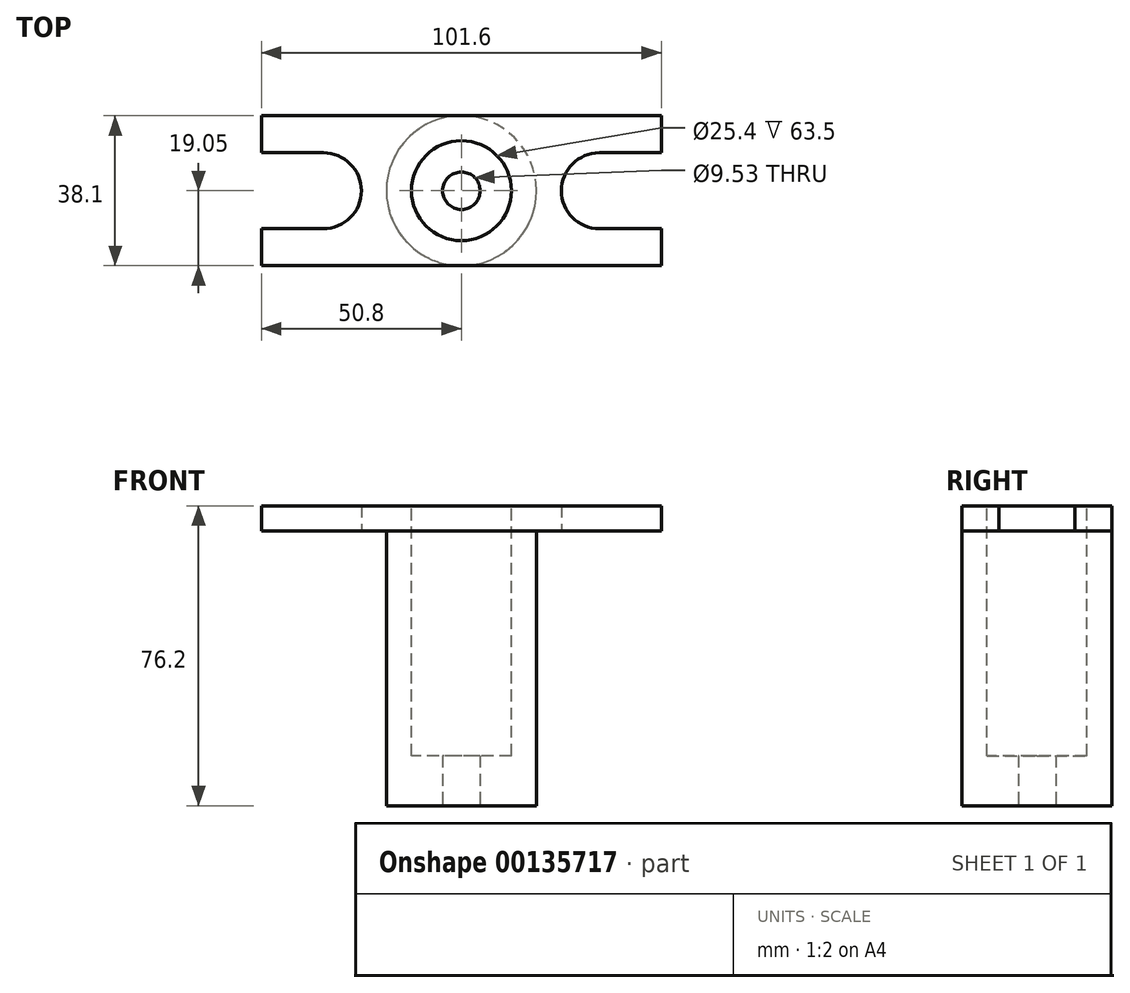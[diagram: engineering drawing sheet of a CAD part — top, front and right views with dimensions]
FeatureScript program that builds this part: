
annotation { "Feature Type Name" : "Feature", "Feature Type Description" : "" }
export const myFeature = defineFeature(function(context is Context, id is Id, definition is map)
    precondition{}
    {
        {
            var Q0;
            Q0=qCreatedBy(makeId("Top.planeOp"),FACE);
            var sketch = newSketch(context, id + "F0", { "sketchPlane" : qUnion([Q0])});
            skLineSegment(sketch, "E0.bottom", {"start": v(0, 0) * mm, "end": v(101.6, 0) * mm});
            skLineSegment(sketch, "E0.top", {"start": v(0, 38.1) * mm, "end": v(101.6, 38.1) * mm});
            skLineSegment(sketch, "E0.left", {"start": v(0, 0) * mm, "end": v(0, 38.1) * mm});
            skLineSegment(sketch, "E0.right", {"start": v(101.6, 0) * mm, "end": v(101.6, 38.1) * mm});
            skSolve(sketch);
        }
        {
            var Q0;
            Q0 = qSketchRegion(id + "F0", true);
            extrude(context, id + "F1", {"entities" : qUnion([Q0]), "depth" : 6.35 * mm});
        }
        {
            var Q0;
            Q0=qCreatedBy(makeId("Top.planeOp"),FACE);
            var sketch = newSketch(context, id + "F2", { "sketchPlane" : qUnion([Q0])});
            skLineSegment(sketch, "E1", {"start": v(0, 28.7) * mm, "end": v(15.75, 28.7) * mm});
            skLineSegment(sketch, "E2", {"start": v(0, 9.4) * mm, "end": v(15.75, 9.4) * mm});
            skArc(sketch, "E3", {"start": v(15.75, 9.4) * mm, "mid": v(25.4, 19.05) * mm, "end": v(15.75, 28.7) * mm});
            skLineSegment(sketch, "E4", {"start": v(0, 28.7) * mm, "end": v(0, 9.4) * mm});
            skLineSegment(sketch, "E5", {"start": v(101.6, 28.7) * mm, "end": v(85.85, 28.7) * mm});
            skLineSegment(sketch, "E6", {"start": v(101.6, 9.4) * mm, "end": v(85.85, 9.4) * mm});
            skArc(sketch, "E7", {"start": v(85.85, 28.7) * mm, "mid": v(76.2, 19.05) * mm, "end": v(85.85, 9.4) * mm});
            skLineSegment(sketch, "E8", {"start": v(101.6, 28.7) * mm, "end": v(101.6, 9.4) * mm});
            skSolve(sketch);
        }
        {
            var Q0;
            Q0 = qSketchRegion(id + "F2", true);
            extrude(context, id + "F3", {"entities" : qUnion([Q0]), "operationType" : NewBodyOperationType.REMOVE, "depth" : 25.4 * mm});
        }
        {
            var Q0;
            Q0=makeQuery(id+"F0.imprint","IMPRINT",FACE,{"disambiguationData":[TD([[makeQuery(id+"F0.imprint","IMPRINT",EDGE,{"derivedFrom":sQuery(id+"F0.wireOp",EDGE,"E0.bottom")}),1.0]])]});
            var sketch = newSketch(context, id + "F4", { "sketchPlane" : qUnion([Q0])});
            skCircle(sketch, "E9", {"center": v(50.8, 19.05) * mm, "radius": 19.05 * mm});
            skSolve(sketch);
        }
        {
            var Q0;
            Q0 = qSketchRegion(id + "F4", true);
            extrude(context, id + "F5", {"entities" : qUnion([Q0]), "operationType" : NewBodyOperationType.ADD, "oppositeDirection" : true, "depth" : 69.85 * mm});
        }
        {
            var Q0;
            Q0=makeQuery(id+"F1.opExtrude","CAP_FACE",FACE,{"disambiguationData":[OSD([sQuery(id+"F0.wireOp",EDGE,"E0.bottom"),sQuery(id+"F0.wireOp",EDGE,"E0.top"),sQuery(id+"F0.wireOp",EDGE,"E0.left"),sQuery(id+"F0.wireOp",EDGE,"E0.right")])],"isStart":false});
            var sketch = newSketch(context, id + "F6", { "sketchPlane" : qUnion([Q0])});
            skCircle(sketch, "E10", {"center": v(50.8, 19.05) * mm, "radius": 12.7 * mm});
            skSolve(sketch);
        }
        {
            var Q0;
            Q0 = qSketchRegion(id + "F6", true);
            extrude(context, id + "F7", {"entities" : qUnion([Q0]), "operationType" : NewBodyOperationType.REMOVE, "oppositeDirection" : true, "depth" : 63.5 * mm});
        }
        {
            var Q0;
            Q0=makeQuery(id+"F5.opExtrude","CAP_FACE",FACE,{"disambiguationData":[OSD([sQuery(id+"F4.wireOp",EDGE,"E9")])],"isStart":false});
            var sketch = newSketch(context, id + "F8", { "sketchPlane" : qUnion([Q0])});
            skCircle(sketch, "E11", {"center": v(50.8, -19.05) * mm, "radius": 4.76 * mm});
            skSolve(sketch);
        }
        {
            var Q0;
            Q0 = qSketchRegion(id + "F8", true);
            extrude(context, id + "F9", {"entities" : qUnion([Q0]), "operationType" : NewBodyOperationType.REMOVE, "endBound" : BoundingType.THROUGH_ALL, "oppositeDirection" : true, "depth" : 6.35 * mm});
        }
    });
